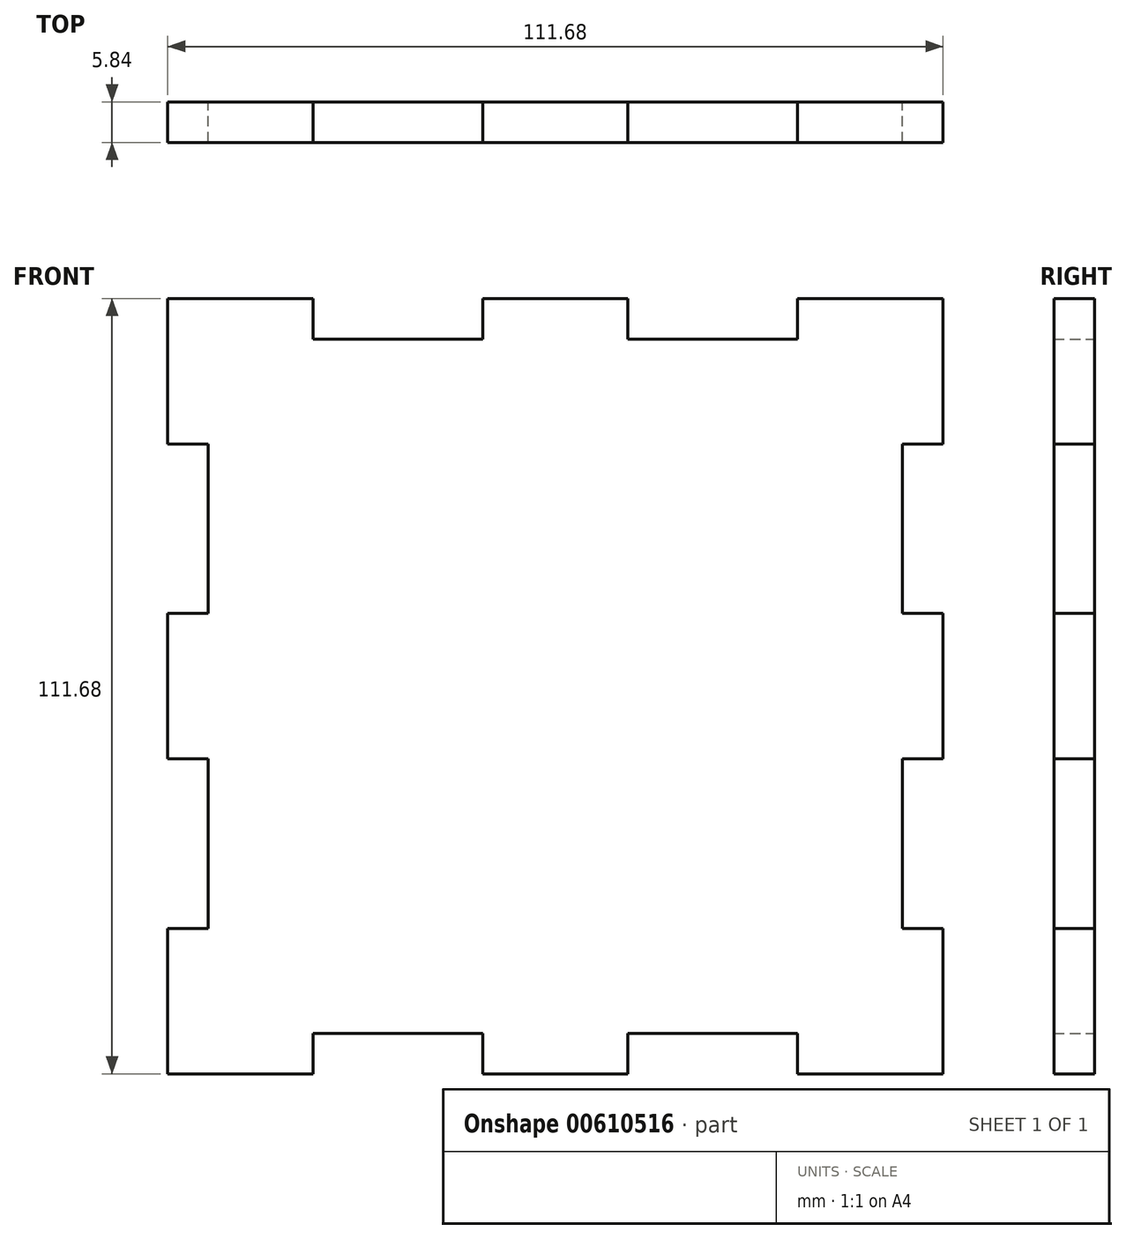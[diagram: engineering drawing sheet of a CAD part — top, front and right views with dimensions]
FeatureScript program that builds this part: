
annotation { "Feature Type Name" : "Feature", "Feature Type Description" : "" }
export const myFeature = defineFeature(function(context is Context, id is Id, definition is map)
    precondition{}
    {
        {
            var Q0;
            Q0=qCreatedBy(makeId("Front.planeOp"),FACE);
            var sketch = newSketch(context, id + "F0", { "sketchPlane" : qUnion([Q0])});
            skLineSegment(sketch, "E0.bottom", {"start": v(50, 50) * mm, "end": v(-50, 50) * mm});
            skLineSegment(sketch, "E0.top", {"start": v(50, -50) * mm, "end": v(-50, -50) * mm});
            skLineSegment(sketch, "E0.left", {"start": v(50, 50) * mm, "end": v(50, -50) * mm});
            skLineSegment(sketch, "E0.right", {"start": v(-50, 50) * mm, "end": v(-50, -50) * mm});
            skPoint(sketch, "E0.middle", {"position": v(0, 0) * mm});
            skLineSegment(sketch, "E1.bottom", {"start": v(-55.84, 55.84) * mm, "end": v(-34.9, 55.84) * mm});
            skLineSegment(sketch, "E1.top", {"start": v(-55.84, -55.84) * mm, "end": v(-34.9, -55.84) * mm});
            skLineSegment(sketch, "E1.left", {"start": v(-55.84, 55.84) * mm, "end": v(-55.84, 34.9) * mm});
            skLineSegment(sketch, "E1.right", {"start": v(55.84, 55.84) * mm, "end": v(55.84, 34.9) * mm});
            skLineSegment(sketch, "E2.bottom", {"start": v(-10.47, 50) * mm, "end": v(10.47, 50) * mm});
            skLineSegment(sketch, "E2.top", {"start": v(-10.47, 55.84) * mm, "end": v(10.47, 55.84) * mm});
            skLineSegment(sketch, "E2.left", {"start": v(-10.47, 50) * mm, "end": v(-10.47, 55.84) * mm});
            skLineSegment(sketch, "E2.right", {"start": v(10.47, 50) * mm, "end": v(10.47, 55.84) * mm});
            skLineSegment(sketch, "E3.right", {"start": v(-34.9, 55.84) * mm, "end": v(-34.9, 50) * mm});
            skLineSegment(sketch, "E4.top", {"start": v(10.47, 50) * mm, "end": v(34.9, 50) * mm});
            skLineSegment(sketch, "E4.left", {"start": v(10.47, 55.84) * mm, "end": v(10.47, 50) * mm});
            skLineSegment(sketch, "E4.right", {"start": v(34.9, 55.84) * mm, "end": v(34.9, 50) * mm});
            skLineSegment(sketch, "E5.bottom", {"start": v(-50, 34.9) * mm, "end": v(-55.84, 34.9) * mm});
            skLineSegment(sketch, "E5.left", {"start": v(-50, 34.9) * mm, "end": v(-50, 10.47) * mm});
            skLineSegment(sketch, "E6.bottom", {"start": v(-55.84, 55.84) * mm, "end": v(-55.84, 55.84) * mm});
            skLineSegment(sketch, "E6.top", {"start": v(-55.84, 34.9) * mm, "end": v(-50, 34.9) * mm});
            skLineSegment(sketch, "E7.bottom", {"start": v(-55.84, -34.9) * mm, "end": v(-50, -34.9) * mm});
            skLineSegment(sketch, "E8.left", {"start": v(-55.84, -55.84) * mm, "end": v(-55.84, -34.9) * mm});
            skLineSegment(sketch, "E9.top", {"start": v(-10.47, -50) * mm, "end": v(10.47, -50) * mm});
            skLineSegment(sketch, "E9.left", {"start": v(-10.47, -55.84) * mm, "end": v(-10.47, -50) * mm});
            skLineSegment(sketch, "E9.right", {"start": v(10.47, -55.84) * mm, "end": v(10.47, -50) * mm});
            skLineSegment(sketch, "E10.top", {"start": v(-10.47, -50) * mm, "end": v(-34.9, -50) * mm});
            skLineSegment(sketch, "E10.right", {"start": v(-34.9, -55.84) * mm, "end": v(-34.9, -50) * mm});
            skLineSegment(sketch, "E11.top", {"start": v(10.47, -50) * mm, "end": v(34.9, -50) * mm});
            skLineSegment(sketch, "E11.right", {"start": v(34.9, -55.84) * mm, "end": v(34.9, -50) * mm});
            skLineSegment(sketch, "E12.bottom", {"start": v(34.9, -55.84) * mm, "end": v(55.84, -55.84) * mm});
            skLineSegment(sketch, "E13.bottom", {"start": v(56.02, -55.84) * mm, "end": v(55.84, -55.84) * mm});
            skLineSegment(sketch, "E13.top", {"start": v(55.84, -34.9) * mm, "end": v(50, -34.9) * mm});
            skLineSegment(sketch, "E13.left", {"start": v(55.84, -55.84) * mm, "end": v(55.84, -34.9) * mm});
            skLineSegment(sketch, "E14.top", {"start": v(55.84, -10.47) * mm, "end": v(50, -10.47) * mm});
            skLineSegment(sketch, "E15.bottom", {"start": v(50, -10.47) * mm, "end": v(55.84, -10.47) * mm});
            skLineSegment(sketch, "E15.top", {"start": v(50, 10.47) * mm, "end": v(55.84, 10.47) * mm});
            skLineSegment(sketch, "E16.top", {"start": v(50, 34.9) * mm, "end": v(55.84, 34.9) * mm});
            skLineSegment(sketch, "E17.trimOffspring", {"start": v(34.9, 55.84) * mm, "end": v(55.84, 55.84) * mm});
            skLineSegment(sketch, "E18.trimOffspring", {"start": v(55.84, 10.47) * mm, "end": v(55.84, -10.47) * mm});
            skLineSegment(sketch, "E19.trimOffspring", {"start": v(55.84, -34.9) * mm, "end": v(55.84, -55.84) * mm});
            skLineSegment(sketch, "E20.trimOffspring", {"start": v(-10.47, -55.84) * mm, "end": v(10.47, -55.84) * mm});
            skLineSegment(sketch, "E21.trimOffspring", {"start": v(-55.84, -34.9) * mm, "end": v(-55.84, -55.84) * mm});
            skLineSegment(sketch, "E22.bottom", {"start": v(-55.84, 10.47) * mm, "end": v(-50, 10.47) * mm});
            skLineSegment(sketch, "E22.top", {"start": v(-55.84, -10.47) * mm, "end": v(-50, -10.47) * mm});
            skLineSegment(sketch, "E22.left", {"start": v(-55.84, 10.47) * mm, "end": v(-55.84, -10.47) * mm});
            skLineSegment(sketch, "E22.right", {"start": v(-50, 10.47) * mm, "end": v(-50, -10.47) * mm});
            skSolve(sketch);
        }
        {
            var Q0;
            Q0 = qSketchRegion(id + "F0", true);
            extrude(context, id + "F1", {"entities" : qUnion([Q0]), "depth" : 5.84 * mm, "offsetDistance" : 25 * mm});
        }
    });
